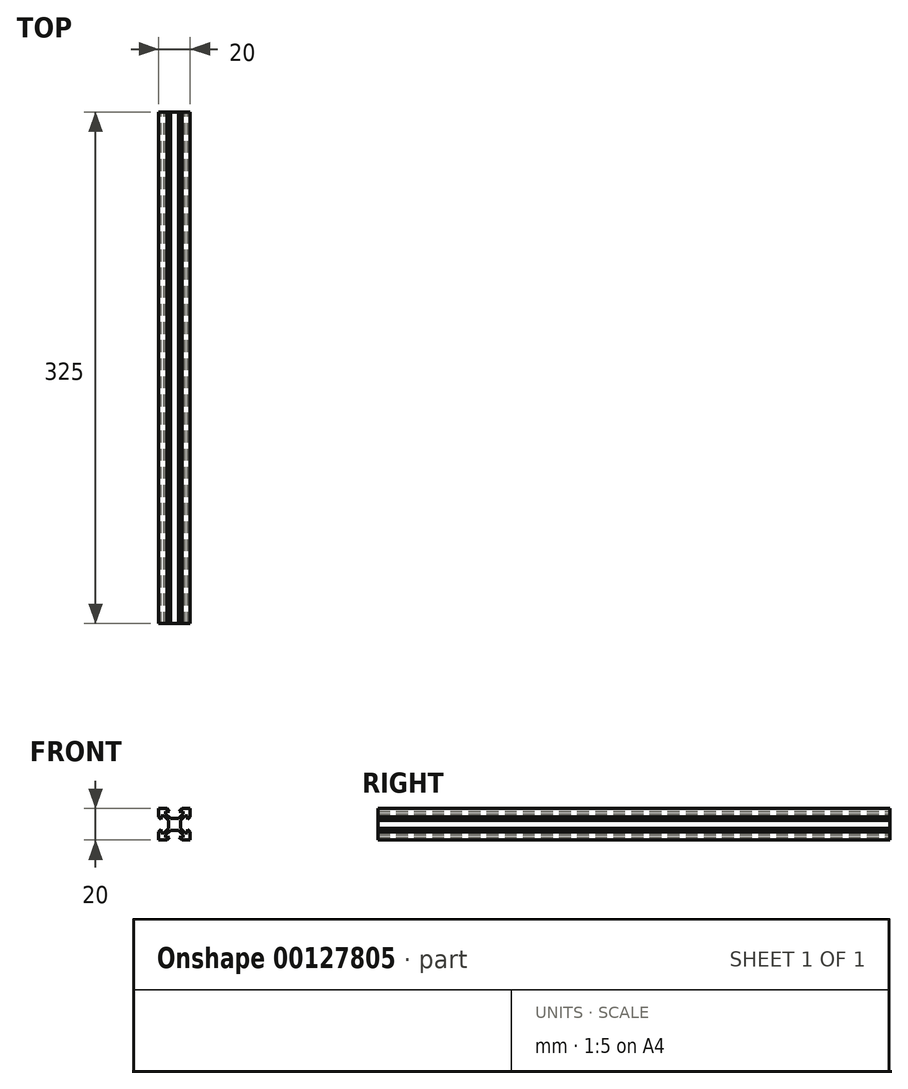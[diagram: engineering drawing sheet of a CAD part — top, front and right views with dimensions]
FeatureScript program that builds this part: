
annotation { "Feature Type Name" : "Feature", "Feature Type Description" : "" }
export const myFeature = defineFeature(function(context is Context, id is Id, definition is map)
    precondition{}
    {
        {
            var Q0;
            Q0=qCreatedBy(makeId("Front.planeOp"),FACE);
            var sketch = newSketch(context, id + "F0", { "sketchPlane" : qUnion([Q0])});
            skLineSegment(sketch, "E0", {"start": v(-10, 10) * mm, "end": v(-4.78, 10) * mm});
            skLineSegment(sketch, "E1", {"start": v(-4.78, 10) * mm, "end": v(-3.1, 8.33) * mm});
            skLineSegment(sketch, "E2", {"start": v(-3.1, 8.32) * mm, "end": v(-5.5, 8.32) * mm});
            skLineSegment(sketch, "E3", {"start": v(-5.5, 8.32) * mm, "end": v(-5.5, 6.68) * mm});
            skLineSegment(sketch, "E4", {"start": v(-5.5, 6.68) * mm, "end": v(-2.57, 3.75) * mm});
            skLineSegment(sketch, "E5", {"start": v(-2.57, 3.75) * mm, "end": v(0, 3.75) * mm});
            skLineSegment(sketch, "E6", {"start": v(0, 0) * mm, "end": v(0, -2.66) * mm, "construction": true});
            skLineSegment(sketch, "E7", {"start": v(0, 0) * mm, "end": v(-3.75, 0) * mm, "construction": true});
            skLineSegment(sketch, "E8", {"start": v(-10, 10) * mm, "end": v(-10, 4.77) * mm});
            skLineSegment(sketch, "E9", {"start": v(-10, 4.78) * mm, "end": v(-8.33, 3.1) * mm});
            skLineSegment(sketch, "E10", {"start": v(-8.32, 3.1) * mm, "end": v(-8.32, 5.5) * mm});
            skLineSegment(sketch, "E11", {"start": v(-8.33, 5.5) * mm, "end": v(-6.68, 5.5) * mm});
            skLineSegment(sketch, "E12", {"start": v(-6.68, 5.5) * mm, "end": v(-3.75, 2.57) * mm});
            skLineSegment(sketch, "E13", {"start": v(-3.75, 2.57) * mm, "end": v(-3.75, 0) * mm});
            skCircle(sketch, "E14", {"center": v(0, 0) * mm, "radius": 2.1 * mm, "construction": true});
            skLineSegment(sketch, "E15.1.0", {"start": v(-5.5, -6.68) * mm, "end": v(-2.57, -3.75) * mm});
            skLineSegment(sketch, "E15.1.1", {"start": v(-5.5, -8.33) * mm, "end": v(-5.5, -6.68) * mm});
            skLineSegment(sketch, "E15.1.2", {"start": v(-3.1, -8.32) * mm, "end": v(-5.5, -8.32) * mm});
            skLineSegment(sketch, "E15.1.3", {"start": v(-4.78, -10) * mm, "end": v(-3.1, -8.33) * mm});
            skLineSegment(sketch, "E15.1.4", {"start": v(-10, -10) * mm, "end": v(-4.77, -10) * mm});
            skLineSegment(sketch, "E15.1.5", {"start": v(-8.32, -5.5) * mm, "end": v(-6.68, -5.5) * mm});
            skLineSegment(sketch, "E15.1.6", {"start": v(-8.32, -3.1) * mm, "end": v(-8.32, -5.5) * mm});
            skLineSegment(sketch, "E15.1.7", {"start": v(-10, -4.77) * mm, "end": v(-8.33, -3.1) * mm});
            skLineSegment(sketch, "E15.1.8", {"start": v(-10, -10) * mm, "end": v(-10, -4.77) * mm});
            skLineSegment(sketch, "E15.1.9", {"start": v(-2.57, -3.75) * mm, "end": v(0, -3.75) * mm});
            skLineSegment(sketch, "E15.1.10", {"start": v(-6.68, -5.5) * mm, "end": v(-3.75, -2.57) * mm});
            skLineSegment(sketch, "E15.1.11", {"start": v(-3.75, -2.57) * mm, "end": v(-3.75, 0) * mm});
            skLineSegment(sketch, "E15.2.0", {"start": v(6.68, -5.5) * mm, "end": v(3.75, -2.57) * mm});
            skLineSegment(sketch, "E15.2.1", {"start": v(8.33, -5.5) * mm, "end": v(6.68, -5.5) * mm});
            skLineSegment(sketch, "E15.2.2", {"start": v(8.32, -3.1) * mm, "end": v(8.32, -5.5) * mm});
            skLineSegment(sketch, "E15.2.3", {"start": v(10, -4.78) * mm, "end": v(8.33, -3.1) * mm});
            skLineSegment(sketch, "E15.2.4", {"start": v(10, -10) * mm, "end": v(10, -4.78) * mm});
            skLineSegment(sketch, "E15.2.5", {"start": v(5.5, -8.32) * mm, "end": v(5.5, -6.68) * mm});
            skLineSegment(sketch, "E15.2.6", {"start": v(3.1, -8.32) * mm, "end": v(5.5, -8.32) * mm});
            skLineSegment(sketch, "E15.2.7", {"start": v(4.77, -10) * mm, "end": v(3.1, -8.33) * mm});
            skLineSegment(sketch, "E15.2.8", {"start": v(10, -10) * mm, "end": v(4.77, -10) * mm});
            skLineSegment(sketch, "E15.2.9", {"start": v(3.75, -2.57) * mm, "end": v(3.75, 0) * mm});
            skLineSegment(sketch, "E15.2.10", {"start": v(5.5, -6.68) * mm, "end": v(2.57, -3.75) * mm});
            skLineSegment(sketch, "E15.2.11", {"start": v(2.57, -3.75) * mm, "end": v(0, -3.75) * mm});
            skLineSegment(sketch, "E15.3.0", {"start": v(5.5, 6.68) * mm, "end": v(2.57, 3.75) * mm});
            skLineSegment(sketch, "E15.3.1", {"start": v(5.5, 8.33) * mm, "end": v(5.5, 6.68) * mm});
            skLineSegment(sketch, "E15.3.2", {"start": v(3.1, 8.32) * mm, "end": v(5.5, 8.32) * mm});
            skLineSegment(sketch, "E15.3.3", {"start": v(4.78, 10) * mm, "end": v(3.1, 8.33) * mm});
            skLineSegment(sketch, "E15.3.4", {"start": v(10, 10) * mm, "end": v(4.78, 10) * mm});
            skLineSegment(sketch, "E15.3.5", {"start": v(8.32, 5.5) * mm, "end": v(6.68, 5.5) * mm});
            skLineSegment(sketch, "E15.3.6", {"start": v(8.32, 3.1) * mm, "end": v(8.32, 5.5) * mm});
            skLineSegment(sketch, "E15.3.7", {"start": v(10, 4.77) * mm, "end": v(8.33, 3.1) * mm});
            skLineSegment(sketch, "E15.3.8", {"start": v(10, 10) * mm, "end": v(10, 4.77) * mm});
            skLineSegment(sketch, "E15.3.9", {"start": v(2.57, 3.75) * mm, "end": v(0, 3.75) * mm});
            skLineSegment(sketch, "E15.3.10", {"start": v(6.68, 5.5) * mm, "end": v(3.75, 2.57) * mm});
            skLineSegment(sketch, "E15.3.11", {"start": v(3.75, 2.57) * mm, "end": v(3.75, 0) * mm});
            skSolve(sketch);
        }
        {
            var Q0;
            Q0 = qSketchRegion(id + "F0", true);
            extrude(context, id + "F1", {"entities" : qUnion([Q0]), "endBound" : BoundingType.SYMMETRIC, "depth" : 325 * mm});
        }
    });
